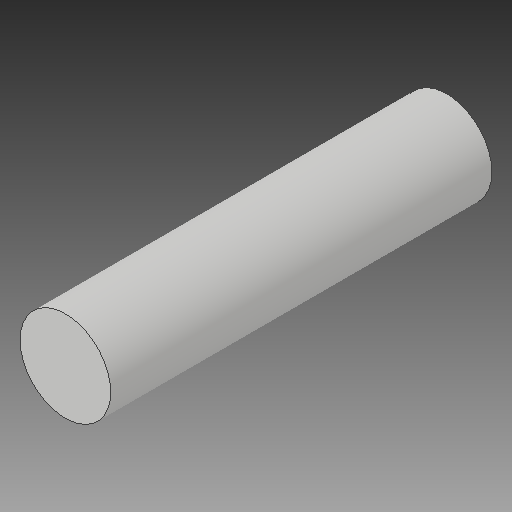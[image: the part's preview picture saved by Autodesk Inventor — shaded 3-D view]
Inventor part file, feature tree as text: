
AUTODESK INVENTOR PART (.ipt)
format: ipt  version: 2018 (Build 220112000, 112)  size: 85,504 bytes
history: native  units: in
note: dims shown in document units (in); Inventor stores cm internally (conversion verified against a paired STEP export)
features: extrude x1, sketch x1
ambient origin geometry x8: Origin, YZ Plane, XZ Plane, XY Plane, X Axis, Y Axis, Z Axis, Center Point
bodies: Solid1 (feature_tree)
feature tree (2):
  extrude  "Extrusion1"  Depth=3.2795in TaperAngle=0.0deg
  sketch  "Sketch1"  dims[d0=0.7795in d1=3.2795in d2=0.0in]
